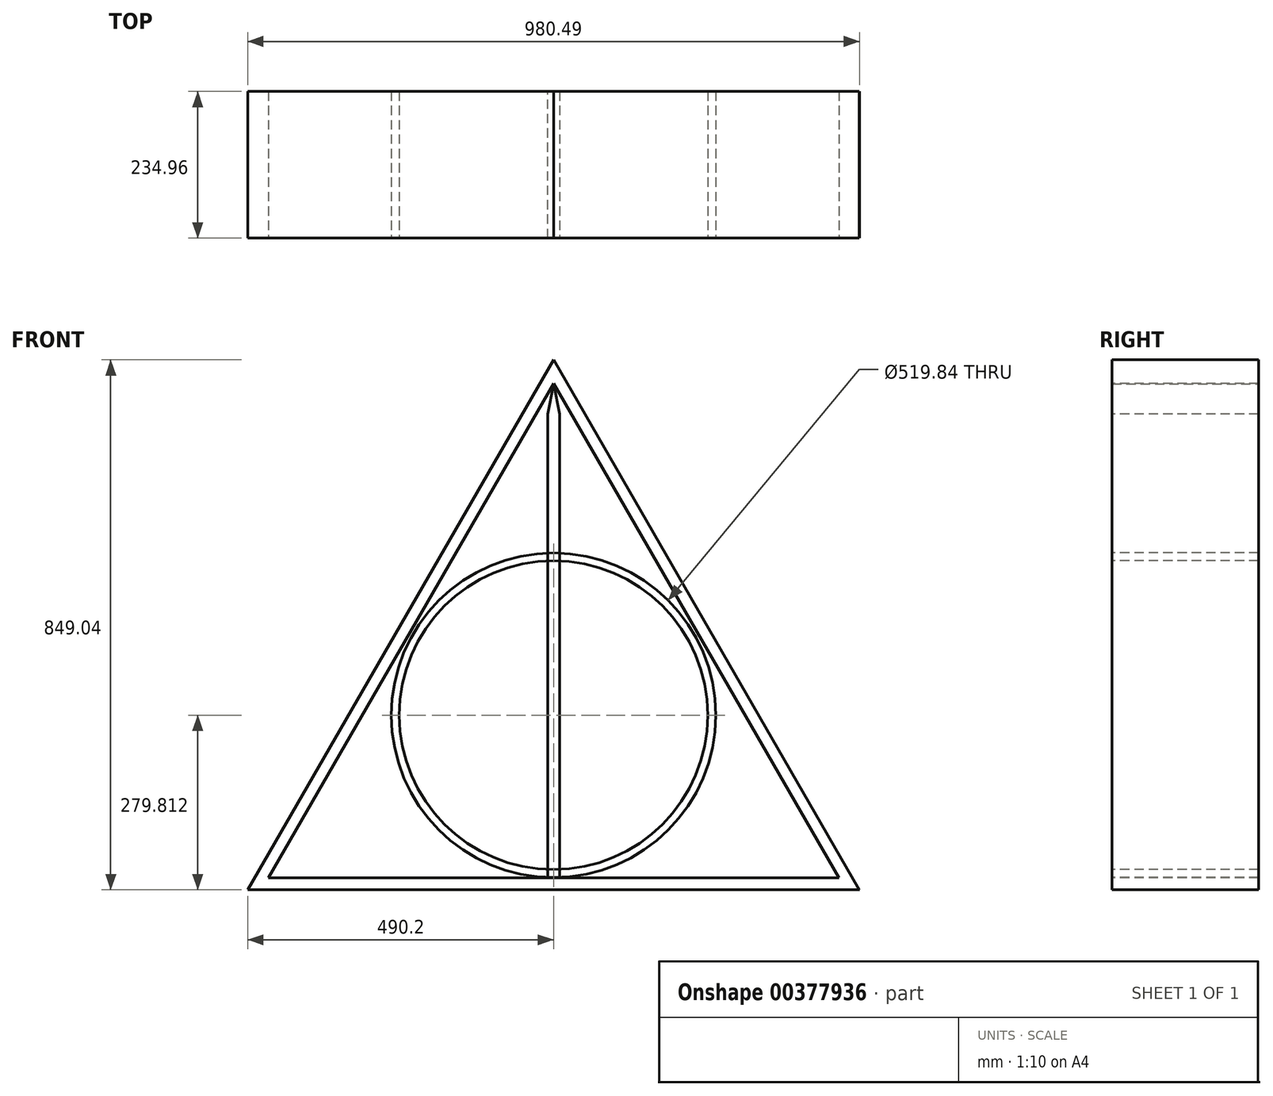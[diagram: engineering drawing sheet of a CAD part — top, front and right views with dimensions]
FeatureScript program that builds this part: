
annotation { "Feature Type Name" : "Feature", "Feature Type Description" : "" }
export const myFeature = defineFeature(function(context is Context, id is Id, definition is map)
    precondition{}
    {
        {
            var Q0;
            Q0=qCreatedBy(makeId("Front.planeOp"),FACE);
            var sketch = newSketch(context, id + "F0", { "sketchPlane" : qUnion([Q0])});
            skLineSegment(sketch, "E0", {"start": v(0, 0) * mm, "end": v(0, 791.9) * mm});
            skLineSegment(sketch, "E1", {"start": v(-457.2, 0) * mm, "end": v(457.2, 0) * mm});
            skLineSegment(sketch, "E2", {"start": v(-457.2, 0) * mm, "end": v(0, 791.9) * mm});
            skLineSegment(sketch, "E3", {"start": v(457.2, 0) * mm, "end": v(0, 791.9) * mm});
            skCircle(sketch, "E4", {"center": v(0, 260.76) * mm, "radius": 247.22 * mm});
            skSolve(sketch);
        }
        {
            var Q0;
            Q0 = qSketchRegion(id + "F0", true);
            var sketch = newSketch(context, id + "F1", { "sketchPlane" : qUnion([Q0])});
            skLineSegment(sketch, "E5.0", {"start": v(-490.2, -19.05) * mm, "end": v(0, 830) * mm});
            skLineSegment(sketch, "E6.0", {"start": v(490, -18.72) * mm, "end": v(0, 830) * mm});
            skLineSegment(sketch, "E7.0", {"start": v(-490.2, -19.05) * mm, "end": v(490.29, -19.05) * mm});
            skLineSegment(sketch, "E8.0", {"start": v(9.53, 0) * mm, "end": v(9.53, 743.44) * mm});
            skLineSegment(sketch, "E9.0", {"start": v(-9.53, 0) * mm, "end": v(-9.53, 743.44) * mm});
            skLineSegment(sketch, "E10", {"start": v(-9.53, 0) * mm, "end": v(9.53, 0) * mm});
            skLineSegment(sketch, "E11", {"start": v(-9.53, 743.44) * mm, "end": v(0, 791.31) * mm});
            skLineSegment(sketch, "E12", {"start": v(9.53, 743.44) * mm, "end": v(0, 791.31) * mm});
            skCircle(sketch, "E13.0", {"center": v(0, 260.76) * mm, "radius": 259.92 * mm});
            skSolve(sketch);
        }
        {
            var Q0;
            Q0 = qSketchRegion(id + "F1", true);
            var sketch = newSketch(context, id + "F2", { "sketchPlane" : qUnion([Q0])});
            skSolve(sketch);
        }
        {
            var Q0;
            Q0 = qSketchRegion(id + "F1", true);
            var Q1;
            Q1=sQuery(id+"F1.wireOp",EDGE,"E13.0");
            extrude(context, id + "F3", {"entities" : qUnion([Q0]), "bodyType" : ToolBodyType.SURFACE, "surfaceEntities" : qUnion([Q1]), "endBound" : BoundingType.SYMMETRIC, "depth" : 234.95 * mm});
        }
        {
            var Q0;
            Q0 = qSketchRegion(id + "F2", true);
            var Q1;
            Q1=sQuery(id+"F1.wireOp",EDGE,"E8.0");
            var Q2;
            Q2=sQuery(id+"F1.wireOp",EDGE,"E9.0");
            extrude(context, id + "F4", {"entities" : qUnion([Q0]), "bodyType" : ToolBodyType.SURFACE, "surfaceEntities" : qUnion([Q1, Q2]), "endBound" : BoundingType.SYMMETRIC, "depth" : 234.95 * mm});
        }
        {
            var Q0;
            {var subQ9=sQuery(id+"F1.wireOp",EDGE,"E11");Q0=makeQuery(id+"F1.imprint","IMPRINT",FACE,{"disambiguationData":[TD([[makeQuery(id+"F1.imprint","IMPRINT",EDGE,{"derivedFrom":subQ9}),1.0]])]});}
            var Q1;
            {var subQ0=sQuery(id+"F1.wireOp",EDGE,"E9.0");var subQ1=sQuery(id+"F0.wireOp",EDGE,"E4");var subQ2=sQuery(id+"F0.wireOp",EDGE,"E0");var subQ3=makeQuery(id+"F0.imprint","IMPRINT",EDGE,{"disambiguationData":[TD([[makeQuery(id+"F0.imprint","INTERSECT",VERTEX,{"disambiguationData":[OD(0.0)],"derivedFrom":[subQ2,subQ1]}),1.0]])],"derivedFrom":subQ1});var subQ4=makeQuery(id+"F1.imprint","INTERSECT",VERTEX,{"disambiguationData":[OD(0.0)],"derivedFrom":[subQ3,subQ0]});Q1=makeQuery(id+"F1.imprint","IMPRINT",FACE,{"disambiguationData":[TD([[makeQuery(id+"F1.imprint","IMPRINT",EDGE,{"disambiguationData":[TD([[subQ4,-1.0]])],"derivedFrom":subQ0}),1.0]])]});}
            var Q2;
            {var subQ0=sQuery(id+"F1.wireOp",EDGE,"E13.0");var subQ1=sQuery(id+"F1.wireOp",EDGE,"E8.0");var subQ2=makeQuery(id+"F1.imprint","INTERSECT",VERTEX,{"disambiguationData":[OD(0.0)],"derivedFrom":[subQ1,subQ0]});Q2=makeQuery(id+"F1.imprint","IMPRINT",FACE,{"disambiguationData":[TD([[makeQuery(id+"F1.imprint","IMPRINT",EDGE,{"disambiguationData":[TD([[subQ2,-1.0]])],"derivedFrom":subQ1}),1.0]])]});}
            var Q3;
            {var subQ1=sQuery(id+"F1.wireOp",EDGE,"E8.0");var subQ6=sQuery(id+"F1.wireOp",EDGE,"E13.0");var subQ7=makeQuery(id+"F1.imprint","INTERSECT",VERTEX,{"disambiguationData":[OD(0.0)],"derivedFrom":[subQ1,subQ6]});Q3=makeQuery(id+"F1.imprint","IMPRINT",FACE,{"disambiguationData":[TD([[makeQuery(id+"F1.imprint","IMPRINT",EDGE,{"disambiguationData":[TD([[subQ7,1.0]])],"derivedFrom":subQ6}),-1.0]])]});}
            var Q4;
            {var subQ0=sQuery(id+"F1.wireOp",EDGE,"E13.0");var subQ1=sQuery(id+"F1.wireOp",EDGE,"E8.0");var subQ2=makeQuery(id+"F1.imprint","INTERSECT",VERTEX,{"disambiguationData":[OD(0.0)],"derivedFrom":[subQ1,subQ0]});Q4=makeQuery(id+"F1.imprint","IMPRINT",FACE,{"disambiguationData":[TD([[makeQuery(id+"F1.imprint","IMPRINT",EDGE,{"disambiguationData":[TD([[subQ2,-1.0]])],"derivedFrom":subQ0}),1.0]])]});}
            var Q5;
            {var subQ1=sQuery(id+"F1.wireOp",EDGE,"E9.0");var subQ6=sQuery(id+"F1.wireOp",EDGE,"E13.0");var subQ7=makeQuery(id+"F1.imprint","INTERSECT",VERTEX,{"disambiguationData":[OD(0.0)],"derivedFrom":[subQ1,subQ6]});Q5=makeQuery(id+"F1.imprint","IMPRINT",FACE,{"disambiguationData":[TD([[makeQuery(id+"F1.imprint","IMPRINT",EDGE,{"disambiguationData":[TD([[subQ7,-1.0]])],"derivedFrom":subQ6}),-1.0]])]});}
            var Q6;
            {var subQ0=sQuery(id+"F1.wireOp",EDGE,"E13.0");var subQ1=sQuery(id+"F1.wireOp",EDGE,"E9.0");var subQ2=makeQuery(id+"F1.imprint","INTERSECT",VERTEX,{"disambiguationData":[OD(1.0)],"derivedFrom":[subQ1,subQ0]});Q6=makeQuery(id+"F1.imprint","IMPRINT",FACE,{"disambiguationData":[TD([[makeQuery(id+"F1.imprint","IMPRINT",EDGE,{"disambiguationData":[TD([[subQ2,1.0]])],"derivedFrom":subQ1}),-1.0]])]});}
            var Q7;
            {var subQ0=sQuery(id+"F1.wireOp",EDGE,"E13.0");var subQ1=sQuery(id+"F1.wireOp",EDGE,"E9.0");var subQ2=makeQuery(id+"F1.imprint","INTERSECT",VERTEX,{"disambiguationData":[OD(0.0)],"derivedFrom":[subQ1,subQ0]});Q7=makeQuery(id+"F1.imprint","IMPRINT",FACE,{"disambiguationData":[TD([[makeQuery(id+"F1.imprint","IMPRINT",EDGE,{"disambiguationData":[TD([[subQ2,1.0]])],"derivedFrom":subQ0}),1.0]])]});}
            var Q8;
            {var subQ0=sQuery(id+"F1.wireOp",EDGE,"E13.0");var subQ1=sQuery(id+"F1.wireOp",EDGE,"E8.0");var subQ2=makeQuery(id+"F1.imprint","INTERSECT",VERTEX,{"disambiguationData":[OD(1.0)],"derivedFrom":[subQ1,subQ0]});Q8=makeQuery(id+"F1.imprint","IMPRINT",FACE,{"disambiguationData":[TD([[makeQuery(id+"F1.imprint","IMPRINT",EDGE,{"disambiguationData":[TD([[subQ2,1.0]])],"derivedFrom":subQ1}),1.0]])]});}
            var Q9;
            {var subQ0=sQuery(id+"F1.wireOp",EDGE,"E12");Q9=makeQuery(id+"F1.imprint","IMPRINT",FACE,{"disambiguationData":[TD([[makeQuery(id+"F1.imprint","IMPRINT",EDGE,{"derivedFrom":subQ0}),1.0]])]});}
            var Q10;
            {var subQ0=sQuery(id+"F1.wireOp",EDGE,"E13.0");var subQ1=sQuery(id+"F1.wireOp",EDGE,"E9.0");var subQ2=makeQuery(id+"F1.imprint","INTERSECT",VERTEX,{"disambiguationData":[OD(0.0)],"derivedFrom":[subQ1,subQ0]});Q10=makeQuery(id+"F1.imprint","IMPRINT",FACE,{"disambiguationData":[TD([[makeQuery(id+"F1.imprint","IMPRINT",EDGE,{"disambiguationData":[TD([[subQ2,-1.0]])],"derivedFrom":subQ1}),-1.0]])]});}
            var Q11;
            {var subQ0=sQuery(id+"F1.wireOp",EDGE,"E8.0");var subQ1=sQuery(id+"F0.wireOp",EDGE,"E4");var subQ2=sQuery(id+"F0.wireOp",EDGE,"E0");var subQ3=makeQuery(id+"F0.imprint","IMPRINT",EDGE,{"disambiguationData":[TD([[makeQuery(id+"F0.imprint","INTERSECT",VERTEX,{"disambiguationData":[OD(0.0)],"derivedFrom":[subQ2,subQ1]}),-1.0]])],"derivedFrom":subQ1});var subQ4=makeQuery(id+"F1.imprint","INTERSECT",VERTEX,{"disambiguationData":[OD(0.0)],"derivedFrom":[subQ3,subQ0]});Q11=makeQuery(id+"F1.imprint","IMPRINT",FACE,{"disambiguationData":[TD([[makeQuery(id+"F1.imprint","IMPRINT",EDGE,{"disambiguationData":[TD([[subQ4,-1.0]])],"derivedFrom":subQ0}),-1.0]])]});}
            var Q12;
            {var subQ0=sQuery(id+"F0.wireOp",EDGE,"E4");var subQ1=sQuery(id+"F0.wireOp",EDGE,"E0");var subQ2=makeQuery(id+"F0.imprint","INTERSECT",VERTEX,{"disambiguationData":[OD(0.0)],"derivedFrom":[subQ1,subQ0]});var subQ4=makeQuery(id+"F0.imprint","IMPRINT",EDGE,{"disambiguationData":[TD([[subQ2,-1.0]])],"derivedFrom":subQ0});var subQ11=sQuery(id+"F1.wireOp",EDGE,"E8.0");var subQ12=makeQuery(id+"F1.imprint","INTERSECT",VERTEX,{"disambiguationData":[OD(0.0)],"derivedFrom":[subQ4,subQ11]});Q12=makeQuery(id+"F1.imprint","IMPRINT",FACE,{"disambiguationData":[TD([[makeQuery(id+"F1.imprint","IMPRINT",EDGE,{"disambiguationData":[TD([[subQ12,-1.0]])],"derivedFrom":subQ11}),1.0]])]});}
            var Q13;
            Q13=sQuery(id+"F1.wireOp",EDGE,"E11");
            var Q14;
            Q14=sQuery(id+"F1.wireOp",EDGE,"E12");
            var Q15;
            Q15=sQuery(id+"F1.wireOp",EDGE,"E13.0");
            extrude(context, id + "F5", {"entities" : qUnion([Q0, Q1, Q2, Q3, Q4, Q5, Q6, Q7, Q8, Q9, Q10, Q11, Q12]), "bodyType" : ToolBodyType.SURFACE, "surfaceEntities" : qUnion([Q13, Q14, Q15]), "endBound" : BoundingType.SYMMETRIC, "oppositeDirection" : true, "depth" : 234.95 * mm});
        }
        {
            var Q0;
            Q0 = qSketchRegion(id + "F0", true);
            var Q1;
            Q1=sQuery(id+"F0.wireOp",EDGE,"E4");
            extrude(context, id + "F6", {"entities" : qUnion([Q0]), "bodyType" : ToolBodyType.SURFACE, "surfaceEntities" : qUnion([Q1]), "endBound" : BoundingType.SYMMETRIC, "depth" : 234.95 * mm});
        }
        {
            var Q0;
            Q0=sQuery(id+"F1.wireOp",EDGE,"E5.0");
            var Q1;
            Q1=sQuery(id+"F1.wireOp",EDGE,"E6.0");
            var Q2;
            Q2=sQuery(id+"F1.wireOp",EDGE,"E7.0");
            extrude(context, id + "F7", {"bodyType" : ToolBodyType.SURFACE, "surfaceEntities" : qUnion([Q0, Q1, Q2]), "endBound" : BoundingType.SYMMETRIC, "depth" : 234.95 * mm});
        }
        {
            var Q0;
            Q0=sQuery(id+"F0.wireOp",EDGE,"E2");
            var Q1;
            Q1=sQuery(id+"F0.wireOp",EDGE,"E3");
            var Q2;
            Q2=sQuery(id+"F0.wireOp",EDGE,"E1");
            extrude(context, id + "F8", {"bodyType" : ToolBodyType.SURFACE, "surfaceEntities" : qUnion([Q0, Q1, Q2]), "endBound" : BoundingType.SYMMETRIC, "depth" : 234.95 * mm});
        }
    });
